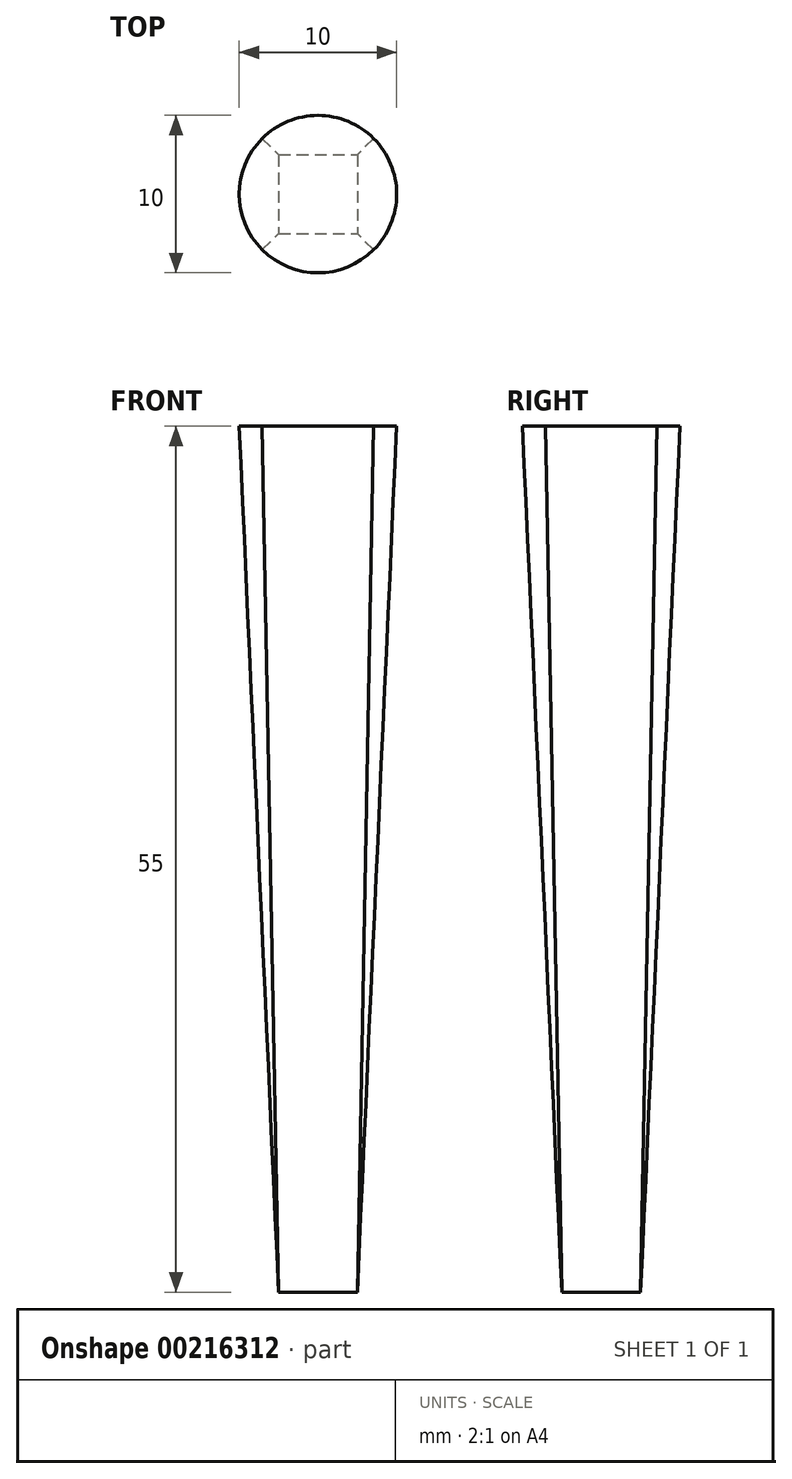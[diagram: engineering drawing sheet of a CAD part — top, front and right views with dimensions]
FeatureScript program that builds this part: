
annotation { "Feature Type Name" : "Feature", "Feature Type Description" : "" }
export const myFeature = defineFeature(function(context is Context, id is Id, definition is map)
    precondition{}
    {
        {
            var Q0;
            Q0=qCreatedBy(makeId("Top.planeOp"),FACE);
            cPlane(context, id + "F0", {"entities" : qUnion([Q0]), "cplaneType" : CPlaneType.OFFSET, "offset" : 55 * mm, "width" : 150 * mm, "height" : 150 * mm});
        }
        {
            var Q0;
            Q0=qCreatedBy(makeId("Top.planeOp"),FACE);
            var sketch = newSketch(context, id + "F1", { "sketchPlane" : qUnion([Q0])});
            skLineSegment(sketch, "E0.bottom", {"start": v(-16.58, 42.26) * mm, "end": v(-11.58, 42.26) * mm});
            skLineSegment(sketch, "E0.top", {"start": v(-16.58, 37.26) * mm, "end": v(-11.58, 37.26) * mm});
            skLineSegment(sketch, "E0.left", {"start": v(-16.58, 42.26) * mm, "end": v(-16.58, 37.26) * mm});
            skLineSegment(sketch, "E0.right", {"start": v(-11.58, 42.26) * mm, "end": v(-11.58, 37.26) * mm});
            skLineSegment(sketch, "E1", {"start": v(-16.58, 42.26) * mm, "end": v(-11.58, 37.26) * mm, "construction": true});
            skSolve(sketch);
        }
        {
            var Q0;
            Q0=qCreatedBy(id+"F0.planeOp",FACE);
            var sketch = newSketch(context, id + "F2", { "sketchPlane" : qUnion([Q0])});
            skCircle(sketch, "E2", {"center": v(-14.08, 39.76) * mm, "radius": 5 * mm});
            skSolve(sketch);
        }
        {
            var Q0;
            Q0=makeQuery(id+"F2.imprint","IMPRINT",FACE,{"disambiguationData":[TD([[makeQuery(id+"F2.imprint","IMPRINT",EDGE,{"derivedFrom":sQuery(id+"F2.wireOp",EDGE,"E2")}),1.0]])]});
            var Q1;
            Q1=makeQuery(id+"F1.imprint","IMPRINT",FACE,{"disambiguationData":[TD([[makeQuery(id+"F1.imprint","IMPRINT",EDGE,{"derivedFrom":sQuery(id+"F1.wireOp",EDGE,"E0.bottom")}),-1.0]])]});
            loft(context, id + "F3", {"sheetProfilesArray" : [{ "sheetProfileEntities" : qUnion([Q0]) }, { "sheetProfileEntities" : qUnion([Q1]) }]});
        }
    });
